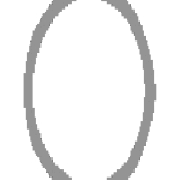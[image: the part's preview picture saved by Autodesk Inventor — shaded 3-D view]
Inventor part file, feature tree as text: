
AUTODESK INVENTOR PART (.ipt)
format: ipt  version: 2021 (Build 250183000, 183)  size: 112,640 bytes
history: native  units: in
note: dims shown in document units (in); Inventor stores cm internally (conversion verified against a paired STEP export)
features: other x4, sketch x3, plane x1
ambient origin geometry x8: Origin, YZ Plane, XZ Plane, XY Plane, X Axis, Y Axis, Z Axis, Center Point
bodies: Solid1 (feature_tree), Body (feature_tree)
feature tree (8):
  other  "Driven Length"
  other  "Frame Generator"
  other  "Start Plane"
  other  "End Plane"
  sketch  "Sketch"  dims[d2=14.0674in d4=-0.0in d5=14.0674in d6=0.12in d7=0.0in d8=90.0deg d9=14.0674in]
  sketch  "Sketch2"  dims[d0=1.0in]
  plane  "Work Plane3"
  sketch  "Sketch3"  dims[d1=0.065in]
